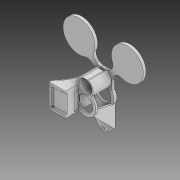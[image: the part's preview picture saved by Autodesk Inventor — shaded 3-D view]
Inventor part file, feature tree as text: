
AUTODESK INVENTOR PART (.ipt)
format: ipt  version: 2020 (Build 240168000, 168)  size: 526,848 bytes
history: native  units: mm
features: extrude x13, sketch x13, chamfer x4, fillet x2
ambient origin geometry x8: Origin, YZ Plane, XZ Plane, XY Plane, X Axis, Y Axis, Z Axis, Center Point
bodies: Solid1 (feature_tree)
feature tree (32):
  extrude  "Extrusion1"  Depth=23.8125mm
  extrude  "Extrusion2"  Depth=3.96875mm
  extrude  "Extrusion3"  Depth=9.797mm
  extrude  "Extrusion4"  Depth=16.1mm
  extrude  "Extrusion13"  Depth=14.15mm
  fillet  "Fillet4"  Radius=18.0mm
  chamfer  "Chamfer2"  Distance=20.0mm
  extrude  "Extrusion15"  Depth=2.0mm
  chamfer  "Chamfer3"  [1 undecoded]
  extrude  "Extrusion16"  Depth=1.0mm
  chamfer  "Chamfer4"  Distance=7.75mm
  extrude  "Extrusion17"  Depth=35.0mm
  extrude  "Extrusion18"  Depth=7.0mm
  extrude  "Extrusion19"  Depth=11.90625mm
  extrude  "Extrusion20"  TaperAngle=45.0deg  [1 undecoded]
  extrude  "Extrusion21"  Depth=26.876241mm
  extrude  "Extrusion22"  Depth=6.0mm
  fillet  "Fillet5"  Radius=3.5mm
  chamfer  "Chamfer5"  Distance=2.5mm
  sketch  "Sketch1"  dims[d0=20.6375mm d1=23.8125mm d2=32.816122mm]
  sketch  "Sketch2"  dims[d3=23.8125mm d4=3.96875mm]
  sketch  "Sketch3"  dims[d5=19.05mm d6=9.797mm]
  sketch  "Sketch4"  dims[d7=5.5mm d8=16.1mm]
  sketch  "Sketch13"  dims[d9=3.0mm d10=0.0mm d11=14.15mm d12=18.0mm d13=8.0mm]
  sketch  "Sketch15"  dims[d14=9.0mm d15=20.0mm d16=0.0mm]
  sketch  "Sketch16"  dims[d17=45.0deg d18=2.0mm d19=0.0mm d20=0.0mm]
  sketch  "Sketch17"  dims[d21=1.0mm d22=1.0mm]
  sketch  "Sketch18"  dims[d23=2.5mm d24=7.75mm d25=0.0mm]
  sketch  "Sketch19"  dims[d58=27.0mm d59=35.0mm]
  sketch  "Sketch20"  dims[d60=1.5mm d61=0.0mm d62=7.0mm]
  sketch  "Sketch21"  dims[d63=0.5mm d64=2.0mm d65=45.0deg d69=11.90625mm]
  sketch  "Sketch22"  dims[d70=45.0deg d71=45.0deg d72=26.876241mm d73=6.0mm d74=3.5mm d75=2.5mm d76=2.0mm d77=0.0mm d78=1.0mm d79=3.0mm d80=45.0deg d81=26.0mm d82=18.0mm d83=35.0mm d84=0.0mm d85=2.0mm d86=2.0mm d87=45.0deg d88=2.4mm d89=20.5mm d90=12.5mm d91=2.5mm d92=20.0mm d93=0.0mm d94=2.0mm d95=0.0mm d96=2.0mm d97=0.0mm d98=2.0mm d99=0.0mm d100=3.0mm d101=5.0mm d102=2.0mm d103=0.0mm d104=27.0mm d105=0.0mm d106=2.0mm d107=0.5mm d108=2.0mm d109=45.0deg]
note: 2 required parameter values undecoded (feature->parameter linkage not recoverable at this tier; creation-order binding heuristic only, values carry confidence <= 0.55)
